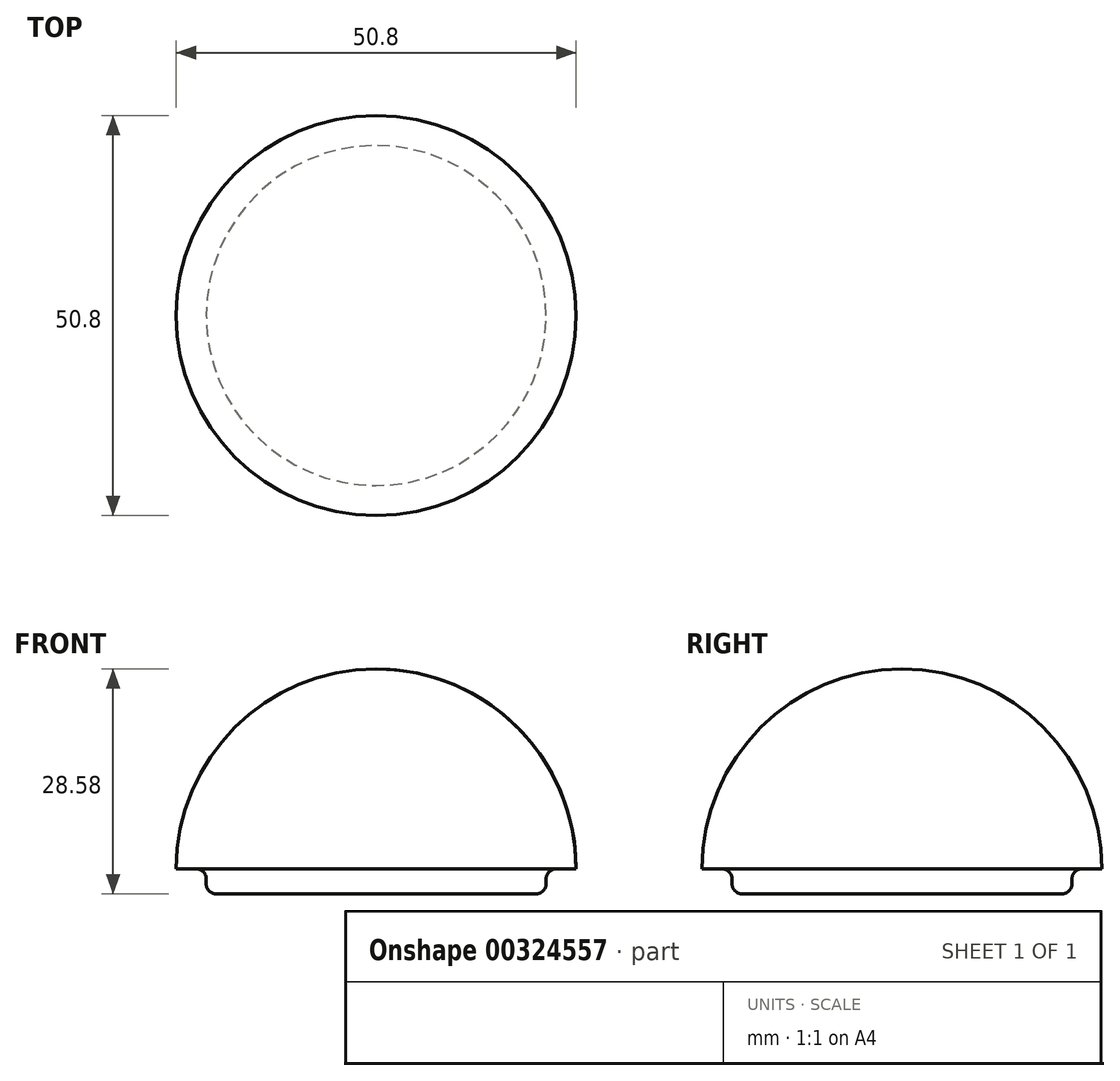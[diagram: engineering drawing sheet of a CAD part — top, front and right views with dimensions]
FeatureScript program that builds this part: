
annotation { "Feature Type Name" : "Feature", "Feature Type Description" : "" }
export const myFeature = defineFeature(function(context is Context, id is Id, definition is map)
    precondition{}
    {
        {
            var Q0;
            Q0=qCreatedBy(makeId("Front.planeOp"),FACE);
            var sketch = newSketch(context, id + "F0", { "sketchPlane" : qUnion([Q0])});
            skLineSegment(sketch, "E0", {"start": v(21.6, -3.17) * mm, "end": v(0, -3.18) * mm});
            skLineSegment(sketch, "E1", {"start": v(0, 25.4) * mm, "end": v(-3.18, 25.4) * mm, "construction": true});
            skLineSegment(sketch, "E2", {"start": v(0, 25.4) * mm, "end": v(0, -3.18) * mm});
            skLineSegment(sketch, "E3", {"start": v(25.4, 0) * mm, "end": v(21.6, 0) * mm});
            skArc(sketch, "E4", {"start": v(25.4, 0) * mm, "mid": v(17.96, 17.96) * mm, "end": v(0, 25.4) * mm});
            skLineSegment(sketch, "E5", {"start": v(21.6, -3.17) * mm, "end": v(21.6, 0) * mm});
            skLineSegment(sketch, "E6", {"start": v(0, 0) * mm, "end": v(0, -3.18) * mm, "construction": true});
            skSolve(sketch);
        }
        {
            var Q0;
            Q0=qSketchRegion(id+"F0",true);
            var Q1;
            Q1=sQuery(id+"F0.wireOp",EDGE,"E2");
            revolve(context, id + "F1", {"entities" : qUnion([Q0]), "axis" : qUnion([Q1]), "revolveType" : RevolveType.FULL});
        }
        {
            var Q0;
            Q0=makeQuery(id+"F1.opRevolve","SWEPT_EDGE",EDGE,{"disambiguationData":[OSD([sQuery(id+"F0.wireOp",EDGE,"E3"),sQuery(id+"F0.wireOp",EDGE,"E5")])]});
            fillet(context, id + "F2", {"entities" : qUnion([Q0]), "radius" : 1.27 * mm, "tangentPropagation" : true, "allowEdgeOverflow" : false});
        }
        {
            var Q0;
            Q0=makeQuery(id+"F1.opRevolve","SWEPT_EDGE",EDGE,{"disambiguationData":[OSD([sQuery(id+"F0.wireOp",EDGE,"E0"),sQuery(id+"F0.wireOp",EDGE,"E5")])]});
            fillet(context, id + "F3", {"entities" : qUnion([Q0]), "radius" : 1.27 * mm, "tangentPropagation" : true, "allowEdgeOverflow" : false});
        }
    });
